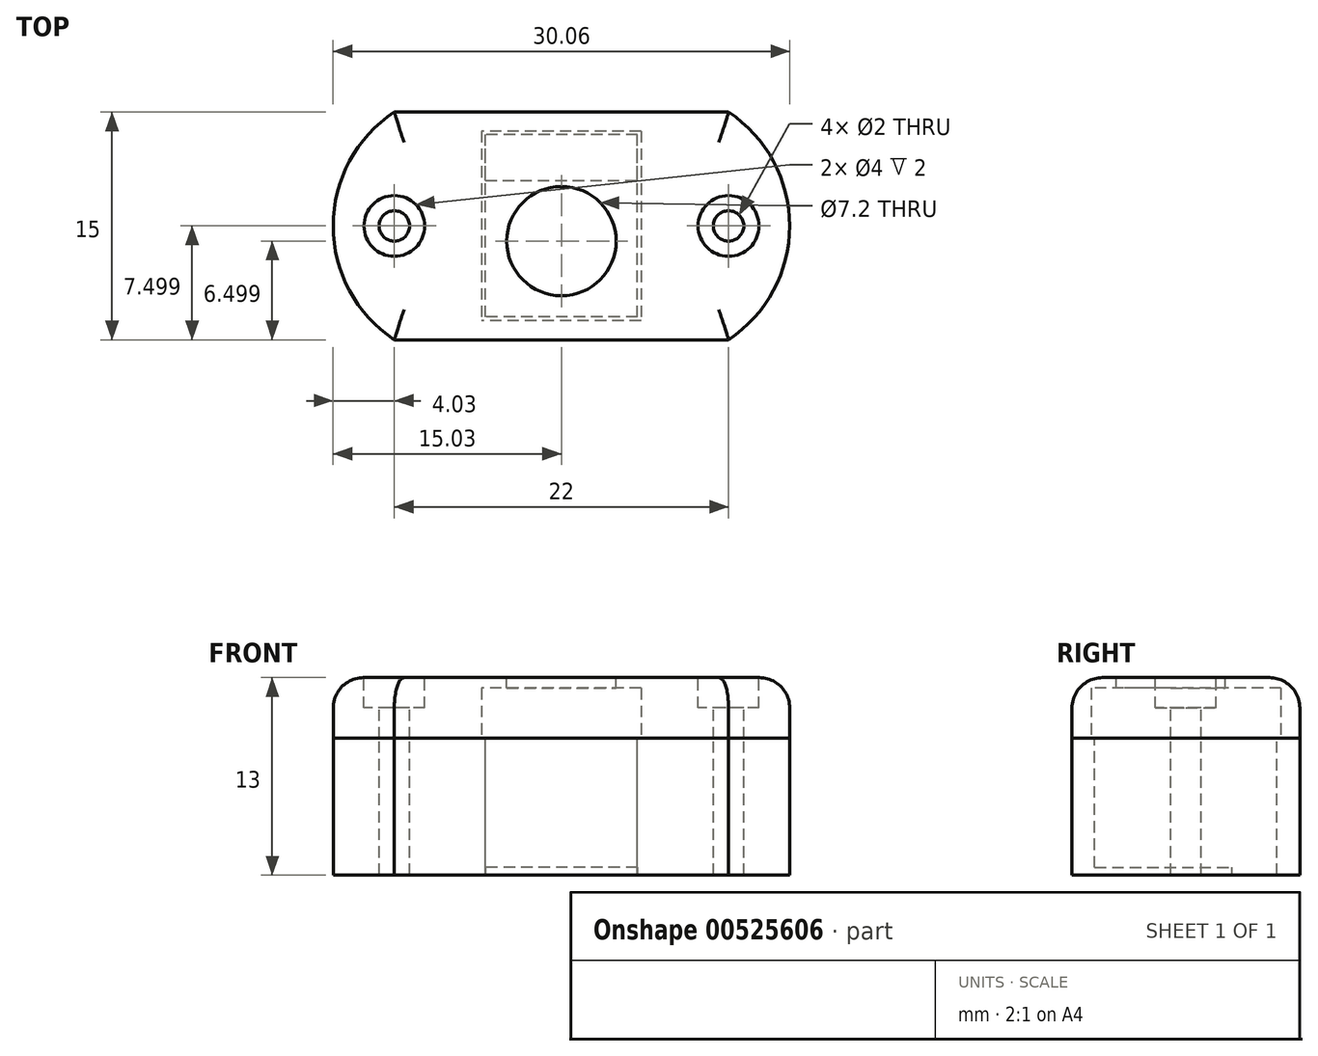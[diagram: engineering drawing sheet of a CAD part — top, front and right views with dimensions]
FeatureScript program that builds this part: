
annotation { "Feature Type Name" : "Feature", "Feature Type Description" : "" }
export const myFeature = defineFeature(function(context is Context, id is Id, definition is map)
    precondition{}
    {
        {
            var Q0;
            Q0=qCreatedBy(makeId("Top.planeOp"),FACE);
            var sketch = newSketch(context, id + "F0", { "sketchPlane" : qUnion([Q0])});
            skLineSegment(sketch, "E0.top", {"start": v(-34, -36.04) * mm, "end": v(-56, -36.04) * mm});
            skLineSegment(sketch, "E0.left", {"start": v(-34, -51.04) * mm, "end": v(-34, -36.04) * mm});
            skLineSegment(sketch, "E0.right", {"start": v(-56, -51.04) * mm, "end": v(-56, -36.04) * mm});
            skPoint(sketch, "E0.middle", {"position": v(-45, -43.54) * mm});
            skArc(sketch, "E1", {"start": v(-34, -51.04) * mm, "mid": v(-29.97, -43.54) * mm, "end": v(-34, -36.04) * mm});
            skArc(sketch, "E2", {"start": v(-56, -36.04) * mm, "mid": v(-60.03, -43.54) * mm, "end": v(-56, -51.04) * mm});
            skLineSegment(sketch, "E3", {"start": v(-56, -51.04) * mm, "end": v(-34, -51.04) * mm});
            skSolve(sketch);
        }
        {
            var Q0;
            Q0=qSketchRegion(id+"F0",true);
            extrude(context, id + "F1", {"entities" : qUnion([Q0]), "depth" : 9 * mm, "offsetDistance" : 25 * mm});
        }
        {
            var Q0;
            Q0=makeQuery(id+"F1.opExtrude","CAP_FACE",FACE,{"disambiguationData":[OSD([sQuery(id+"F0.wireOp",EDGE,"E0.bottom"),sQuery(id+"F0.wireOp",EDGE,"E0.top"),sQuery(id+"F0.wireOp",EDGE,"E0.left"),sQuery(id+"F0.wireOp",EDGE,"E0.right")])],"isStart":false});
            var sketch = newSketch(context, id + "F2", { "sketchPlane" : qUnion([Q0])});
            skCircle(sketch, "E4", {"center": v(-56, -43.54) * mm, "radius": 1 * mm});
            skCircle(sketch, "E5", {"center": v(-34, -43.54) * mm, "radius": 1 * mm});
            skCircle(sketch, "E6", {"center": v(-45, -43.54) * mm, "radius": 3.55 * mm, "construction": true});
            skLineSegment(sketch, "E7.bottom", {"start": v(-40, -49.54) * mm, "end": v(-50, -49.54) * mm});
            skLineSegment(sketch, "E7.top", {"start": v(-40, -37.54) * mm, "end": v(-50, -37.54) * mm});
            skLineSegment(sketch, "E7.left", {"start": v(-40, -49.54) * mm, "end": v(-40, -37.54) * mm});
            skLineSegment(sketch, "E7.right", {"start": v(-50, -49.54) * mm, "end": v(-50, -37.54) * mm});
            skSolve(sketch);
        }
        {
            var Q0;
            Q0=qSketchRegion(id+"F2",true);
            extrude(context, id + "F3", {"entities" : qUnion([Q0]), "operationType" : NewBodyOperationType.REMOVE, "oppositeDirection" : true, "depth" : 9 * mm, "offsetDistance" : 25 * mm});
        }
        {
            var Q0;
            Q0=makeQuery(id+"F1.opExtrude","CAP_FACE",FACE,{"disambiguationData":[OSD([sQuery(id+"F0.wireOp",EDGE,"E0.top"),sQuery(id+"F0.wireOp",EDGE,"E1"),sQuery(id+"F0.wireOp",EDGE,"E2"),sQuery(id+"F0.wireOp",EDGE,"E3")])],"isStart":true});
            var sketch = newSketch(context, id + "F4", { "sketchPlane" : qUnion([Q0])});
            skPoint(sketch, "E8.middle.positionSnap0", {"position": v(-45, 37.54) * mm});
            skPoint(sketch, "E8.centerSnap0", {"position": v(-45, 37.54) * mm});
            skLineSegment(sketch, "E9.bottom", {"start": v(-50, 40.54) * mm, "end": v(-40, 40.54) * mm});
            skLineSegment(sketch, "E9.top", {"start": v(-50, 49.54) * mm, "end": v(-40, 49.54) * mm});
            skLineSegment(sketch, "E9.left", {"start": v(-50, 40.54) * mm, "end": v(-50, 49.54) * mm});
            skLineSegment(sketch, "E9.right", {"start": v(-40, 40.54) * mm, "end": v(-40, 49.54) * mm});
            skSolve(sketch);
        }
        {
            var Q0;
            Q0=qSketchRegion(id+"F4",true);
            extrude(context, id + "F5", {"entities" : qUnion([Q0]), "operationType" : NewBodyOperationType.ADD, "oppositeDirection" : true, "depth" : 0.5 * mm, "offsetDistance" : 25 * mm});
        }
        {
            var Q0;
            Q0=makeQuery(id+"F1.opExtrude","CAP_FACE",FACE,{"disambiguationData":[OSD([sQuery(id+"F0.wireOp",EDGE,"E0.top"),sQuery(id+"F0.wireOp",EDGE,"E1"),sQuery(id+"F0.wireOp",EDGE,"E2"),sQuery(id+"F0.wireOp",EDGE,"E3")])],"isStart":false});
            var sketch = newSketch(context, id + "F6", { "sketchPlane" : qUnion([Q0])});
            skLineSegment(sketch, "E10.top", {"start": v(-34, -36.04) * mm, "end": v(-56, -36.04) * mm});
            skLineSegment(sketch, "E10.left", {"start": v(-34, -51.04) * mm, "end": v(-34, -36.04) * mm});
            skLineSegment(sketch, "E10.right", {"start": v(-56, -51.04) * mm, "end": v(-56, -36.04) * mm});
            skPoint(sketch, "E10.middle", {"position": v(-45, -43.54) * mm});
            skArc(sketch, "E11", {"start": v(-34, -51.04) * mm, "mid": v(-29.97, -43.54) * mm, "end": v(-34, -36.04) * mm});
            skArc(sketch, "E12", {"start": v(-56, -36.04) * mm, "mid": v(-60.03, -43.54) * mm, "end": v(-56, -51.04) * mm});
            skLineSegment(sketch, "E13", {"start": v(-56, -51.04) * mm, "end": v(-34, -51.04) * mm});
            skPoint(sketch, "E14", {"position": v(-40, -43.54) * mm});
            skPoint(sketch, "E15", {"position": v(-45, -37.54) * mm});
            skSolve(sketch);
        }
        {
            var Q0;
            Q0=qSketchRegion(id+"F6",true);
            extrude(context, id + "F7", {"entities" : qUnion([Q0]), "depth" : 4 * mm, "offsetDistance" : 25 * mm});
        }
        {
            var Q0;
            Q0=makeQuery(id+"F7.opExtrude","CAP_FACE",FACE,{"disambiguationData":[OSD([sQuery(id+"F6.wireOp",EDGE,"E10.top"),sQuery(id+"F6.wireOp",EDGE,"E11"),sQuery(id+"F6.wireOp",EDGE,"E12"),sQuery(id+"F6.wireOp",EDGE,"E13")])],"isStart":false});
            var sketch = newSketch(context, id + "F8", { "sketchPlane" : qUnion([Q0])});
            skCircle(sketch, "E16", {"center": v(-56, -43.54) * mm, "radius": 1 * mm, "construction": true});
            skCircle(sketch, "E17", {"center": v(-34, -43.54) * mm, "radius": 1 * mm, "construction": true});
            skPoint(sketch, "E18", {"position": v(-29.97, -43.54) * mm});
            skPoint(sketch, "E19", {"position": v(-45, -51.04) * mm});
            skCircle(sketch, "E20", {"center": v(-45, -44.54) * mm, "radius": 3.6 * mm});
            skSolve(sketch);
        }
        {
            var Q0;
            Q0=qSketchRegion(id+"F8",true);
            extrude(context, id + "F9", {"entities" : qUnion([Q0]), "operationType" : NewBodyOperationType.REMOVE, "oppositeDirection" : true, "depth" : 4 * mm, "offsetDistance" : 25 * mm});
        }
        {
            var Q0;
            Q0=makeQuery(id+"F7.opExtrude","CAP_EDGE",EDGE,{"disambiguationData":[OSD([sQuery(id+"F6.wireOp",EDGE,"E11")])],"isStart":false});
            var Q1;
            Q1=makeQuery(id+"F7.opExtrude","CAP_EDGE",EDGE,{"disambiguationData":[OSD([sQuery(id+"F6.wireOp",EDGE,"E10.top")])],"isStart":false});
            var Q2;
            Q2=makeQuery(id+"F7.opExtrude","CAP_EDGE",EDGE,{"disambiguationData":[OSD([sQuery(id+"F6.wireOp",EDGE,"E12")])],"isStart":false});
            var Q3;
            Q3=makeQuery(id+"F7.opExtrude","CAP_EDGE",EDGE,{"disambiguationData":[OSD([sQuery(id+"F6.wireOp",EDGE,"E13")])],"isStart":false});
            fillet(context, id + "F10", {"entities" : qUnion([Q0, Q1, Q2, Q3]), "radius" : 2 * mm, "tangentPropagation" : true, "allowEdgeOverflow" : false});
        }
        {
            var Q0;
            Q0=sQuery(id+"F8.wireOp",VERTEX,"E17.center");
            var Q1;
            Q1=sQuery(id+"F8.wireOp",VERTEX,"E16.center");
            var Q2;
            Q2=makeQuery(id+"F7.opExtrude","SWEPT_BODY",BODY,{"disambiguationData":[OSD([sQuery(id+"F6.wireOp",EDGE,"E10.top"),sQuery(id+"F6.wireOp",EDGE,"E11"),sQuery(id+"F6.wireOp",EDGE,"E12"),sQuery(id+"F6.wireOp",EDGE,"E13")])]});
            hole(context, id + "F11", {"style" : HoleStyle.C_BORE, "endStyle" : HoleEndStyle.BLIND, "holeDiameter" : 2 * mm, "cBoreDiameter" : 4 * mm, "cBoreDepth" : 2 * mm, "majorDiameter" : 5 * mm, "holeDepth" : 20 * mm, "tappedDepth" : 12 * mm, "tapClearance" : 3, "locations" : qUnion([Q0, Q1]), "scope" : qUnion([Q2])});
        }
        {
            var Q0;
            Q0=makeQuery(id+"F7.opExtrude","CAP_FACE",FACE,{"disambiguationData":[OSD([sQuery(id+"F6.wireOp",EDGE,"E10.top"),sQuery(id+"F6.wireOp",EDGE,"E11"),sQuery(id+"F6.wireOp",EDGE,"E12"),sQuery(id+"F6.wireOp",EDGE,"E13")])],"isStart":true});
            var sketch = newSketch(context, id + "F12", { "sketchPlane" : qUnion([Q0])});
            skLineSegment(sketch, "E21.bottom", {"start": v(-39.75, 37.3) * mm, "end": v(-50.25, 37.3) * mm});
            skLineSegment(sketch, "E21.top", {"start": v(-39.75, 49.8) * mm, "end": v(-50.25, 49.8) * mm});
            skLineSegment(sketch, "E21.left", {"start": v(-39.75, 37.3) * mm, "end": v(-39.75, 49.8) * mm});
            skLineSegment(sketch, "E21.right", {"start": v(-50.25, 37.3) * mm, "end": v(-50.25, 49.8) * mm});
            skPoint(sketch, "E21.middle", {"position": v(-45, 43.54) * mm});
            skSolve(sketch);
        }
        {
            var Q0;
            Q0=qSketchRegion(id+"F12",true);
            extrude(context, id + "F13", {"entities" : qUnion([Q0]), "operationType" : NewBodyOperationType.REMOVE, "oppositeDirection" : true, "depth" : 3.3 * mm, "offsetDistance" : 25 * mm});
        }
    });
